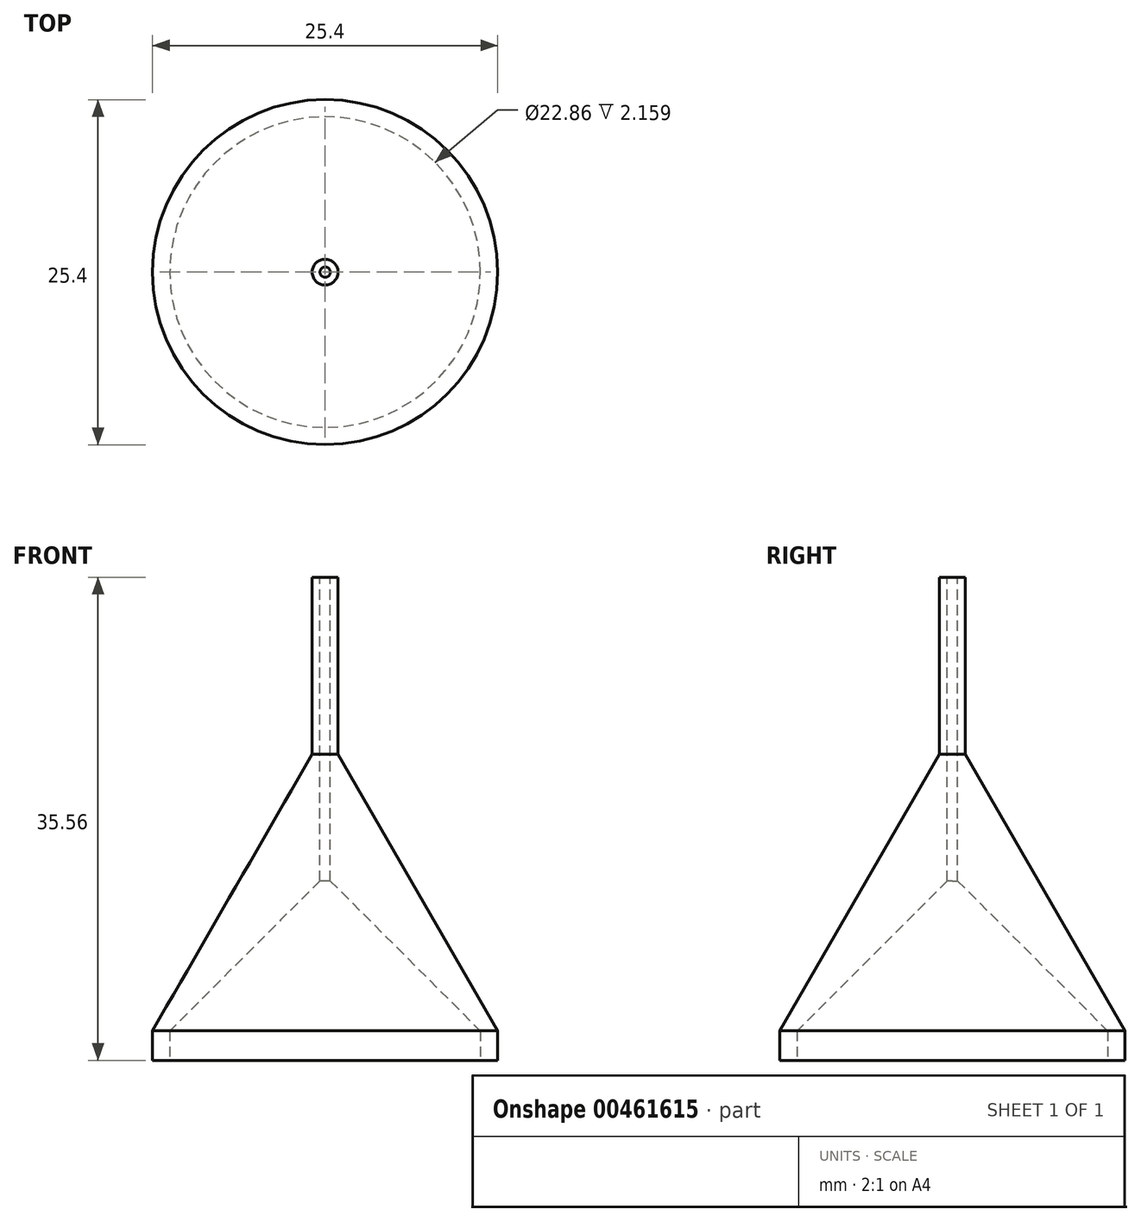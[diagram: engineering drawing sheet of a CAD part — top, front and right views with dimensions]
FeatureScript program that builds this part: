
annotation { "Feature Type Name" : "Feature", "Feature Type Description" : "" }
export const myFeature = defineFeature(function(context is Context, id is Id, definition is map)
    precondition{}
    {
        {
            var Q0;
            Q0=qCreatedBy(makeId("Top.planeOp"),FACE);
            var sketch = newSketch(context, id + "F0", { "sketchPlane" : qUnion([Q0])});
            skCircle(sketch, "E0", {"center": v(-32.79, 35.5) * mm, "radius": 12.7 * mm});
            skSolve(sketch);
        }
        {
            var Q0;
            Q0 = qSketchRegion(id + "F0", true);
            extrude(context, id + "F1", {"entities" : qUnion([Q0]), "depth" : 22.86 * mm});
        }
        {
            var Q0;
            Q0=makeQuery(id+"F1.opExtrude","CAP_FACE",FACE,{"disambiguationData":[OSD([sQuery(id+"F0.wireOp",EDGE,"E0")])],"isStart":false});
            var sketch = newSketch(context, id + "F2", { "sketchPlane" : qUnion([Q0])});
            skCircle(sketch, "E1", {"center": v(-32.79, 35.5) * mm, "radius": 0.95 * mm});
            skSolve(sketch);
        }
        {
            var Q0;
            Q0 = qSketchRegion(id + "F2", true);
            extrude(context, id + "F3", {"entities" : qUnion([Q0]), "operationType" : NewBodyOperationType.ADD, "depth" : 12.7 * mm});
        }
        {
            var Q0;
            Q0=makeQuery(id+"F3.opExtrude","CAP_FACE",FACE,{"disambiguationData":[OSD([sQuery(id+"F2.wireOp",EDGE,"E1")])],"isStart":false});
            var sketch = newSketch(context, id + "F4", { "sketchPlane" : qUnion([Q0])});
            skCircle(sketch, "E2", {"center": v(-32.79, 35.5) * mm, "radius": 0.38 * mm});
            skSolve(sketch);
        }
        {
            var Q0;
            Q0 = qSketchRegion(id + "F4", true);
            extrude(context, id + "F5", {"entities" : qUnion([Q0]), "operationType" : NewBodyOperationType.REMOVE, "endBound" : BoundingType.THROUGH_ALL, "oppositeDirection" : true, "depth" : 25.4 * mm});
        }
        {
            var Q0;
            Q0=makeQuery(id+"F1.opExtrude","CAP_EDGE",EDGE,{"disambiguationData":[OSD([sQuery(id+"F0.wireOp",EDGE,"E0")])],"isStart":false});
            chamfer(context, id + "F6", {"entities" : qUnion([Q0]), "chamferType" : ChamferType.OFFSET_ANGLE, "width" : 11.94 * mm, "oppositeDirection" : false, "angle" : 60 * degree, "tangentPropagation" : true});
        }
        {
            var Q0;
            Q0=makeQuery(id+"F1.opExtrude","CAP_FACE",FACE,{"disambiguationData":[OSD([sQuery(id+"F0.wireOp",EDGE,"E0")])],"isStart":true});
            var sketch = newSketch(context, id + "F7", { "sketchPlane" : qUnion([Q0])});
            skCircle(sketch, "E3", {"center": v(-32.79, -35.5) * mm, "radius": 11.43 * mm});
            skSolve(sketch);
        }
        {
            var Q0;
            Q0 = qSketchRegion(id + "F7", true);
            extrude(context, id + "F8", {"entities" : qUnion([Q0]), "operationType" : NewBodyOperationType.REMOVE, "oppositeDirection" : true, "depth" : 1.27 * mm});
        }
        {
            var Q0;
            Q0=makeQuery(id+"F8.boolean.opBoolean","INTERSECT",EDGE,{"derivedFrom":[makeQuery(id+"F5.boolean.opBoolean","COPY",FACE,{"derivedFrom":makeQuery(id+"F5.opExtrude","SWEPT_FACE",FACE,{"disambiguationData":[OSD([sQuery(id+"F4.wireOp",EDGE,"E2")])]})}),makeQuery(id+"F8.opExtrude","CAP_FACE",FACE,{"disambiguationData":[OSD([sQuery(id+"F7.wireOp",EDGE,"E3")])],"isStart":false})]});
            chamfer(context, id + "F9", {"entities" : qUnion([Q0]), "width" : 11.94 * mm, "tangentPropagation" : true});
        }
    });
